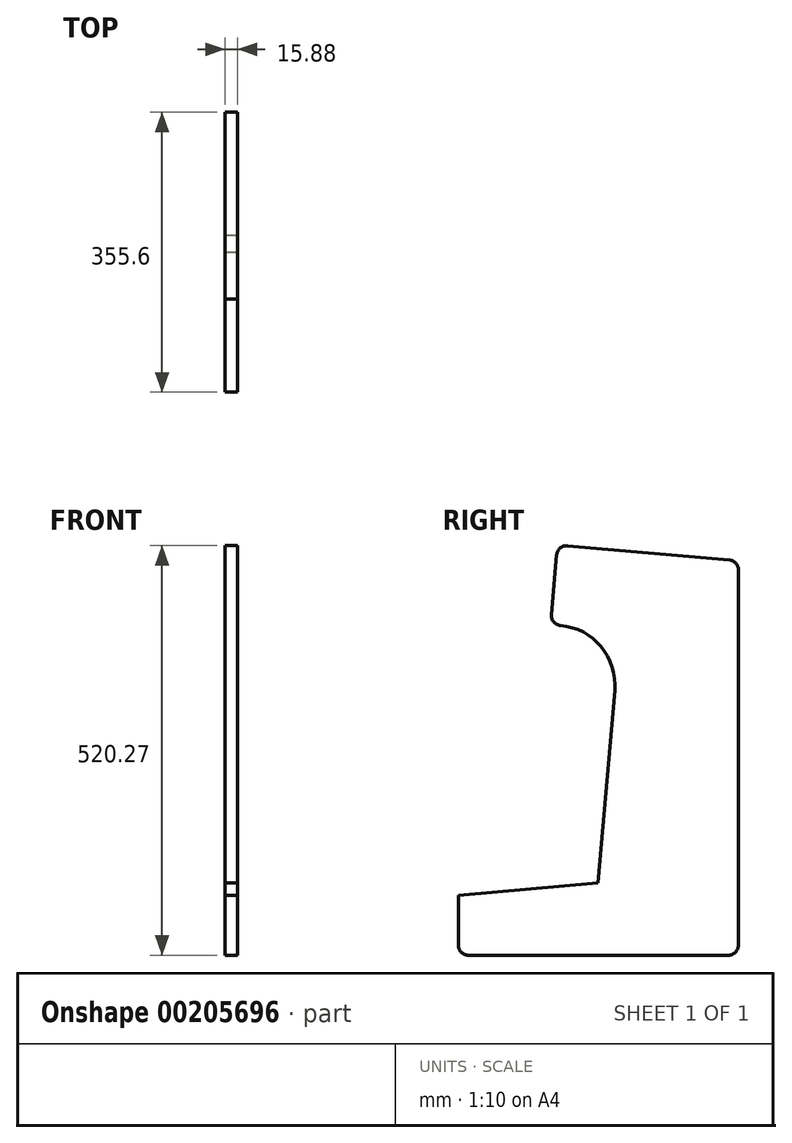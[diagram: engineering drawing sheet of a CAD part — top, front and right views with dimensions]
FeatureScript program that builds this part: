
annotation { "Feature Type Name" : "Feature", "Feature Type Description" : "" }
export const myFeature = defineFeature(function(context is Context, id is Id, definition is map)
    precondition{}
    {
        {
            var Q0;
            Q0=qCreatedBy(makeId("Right.planeOp"),FACE);
            var sketch = newSketch(context, id + "F0", { "sketchPlane" : qUnion([Q0])});
            skLineSegment(sketch, "E0", {"start": v(0, 0) * mm, "end": v(-355.6, 0) * mm});
            skLineSegment(sketch, "E1", {"start": v(-355.6, 0) * mm, "end": v(-355.6, 76.2) * mm});
            skLineSegment(sketch, "E2", {"start": v(-355.6, 76.2) * mm, "end": v(-178.48, 91.7) * mm});
            skLineSegment(sketch, "E3", {"start": v(-178.48, 91.7) * mm, "end": v(-150.42, 412.4) * mm});
            skLineSegment(sketch, "E4", {"start": v(-150.42, 412.4) * mm, "end": v(-238.6, 420.12) * mm});
            skLineSegment(sketch, "E5", {"start": v(-238.6, 420.12) * mm, "end": v(-229.75, 521.33) * mm});
            skLineSegment(sketch, "E6", {"start": v(-229.75, 521.33) * mm, "end": v(0, 501.23) * mm});
            skLineSegment(sketch, "E7", {"start": v(0, 501.23) * mm, "end": v(0, 0) * mm});
            skSolve(sketch);
        }
        {
            var Q0;
            Q0=makeQuery(id+"F0.imprint","IMPRINT",FACE,{"disambiguationData":[TD([[makeQuery(id+"F0.imprint","IMPRINT",EDGE,{"derivedFrom":sQuery(id+"F0.wireOp",EDGE,"E0")}),-1.0]])]});
            extrude(context, id + "F1", {"entities" : qUnion([Q0]), "depth" : 15.88 * mm});
        }
        {
            var Q0;
            Q0=makeQuery(id+"F1.opExtrude","SWEPT_EDGE",EDGE,{"disambiguationData":[OSD([sQuery(id+"F0.wireOp",EDGE,"E0"),sQuery(id+"F0.wireOp",EDGE,"E1")])]});
            var Q1;
            Q1=makeQuery(id+"F1.opExtrude","SWEPT_EDGE",EDGE,{"disambiguationData":[OSD([sQuery(id+"F0.wireOp",EDGE,"E0"),sQuery(id+"F0.wireOp",EDGE,"E7")])]});
            var Q2;
            Q2=makeQuery(id+"F1.opExtrude","SWEPT_EDGE",EDGE,{"disambiguationData":[OSD([sQuery(id+"F0.wireOp",EDGE,"E6"),sQuery(id+"F0.wireOp",EDGE,"E7")])]});
            var Q3;
            Q3=makeQuery(id+"F1.opExtrude","SWEPT_EDGE",EDGE,{"disambiguationData":[OSD([sQuery(id+"F0.wireOp",EDGE,"E4"),sQuery(id+"F0.wireOp",EDGE,"E5")])]});
            var Q4;
            Q4=makeQuery(id+"F1.opExtrude","SWEPT_EDGE",EDGE,{"disambiguationData":[OSD([sQuery(id+"F0.wireOp",EDGE,"E5"),sQuery(id+"F0.wireOp",EDGE,"E6")])]});
            fillet(context, id + "F2", {"entities" : qUnion([Q0, Q1, Q2, Q3, Q4]), "radius" : 12.7 * mm, "tangentPropagation" : true, "allowEdgeOverflow" : false});
        }
        {
            var Q0;
            Q0=makeQuery(id+"F1.opExtrude","SWEPT_EDGE",EDGE,{"disambiguationData":[OSD([sQuery(id+"F0.wireOp",EDGE,"E3"),sQuery(id+"F0.wireOp",EDGE,"E4")])]});
            fillet(context, id + "F3", {"entities" : qUnion([Q0]), "radius" : 76.2 * mm, "tangentPropagation" : true, "allowEdgeOverflow" : false});
        }
    });
